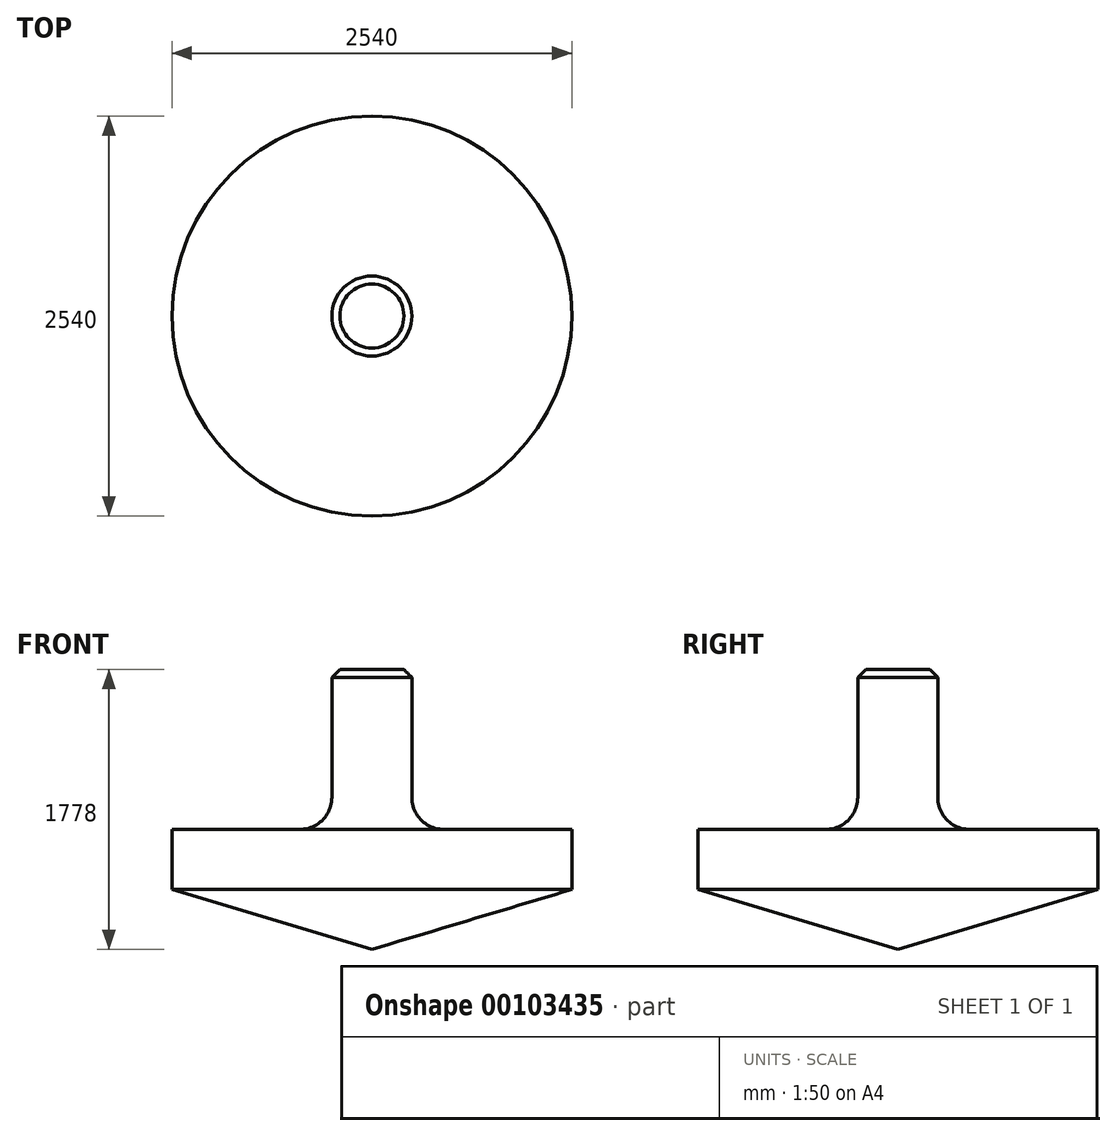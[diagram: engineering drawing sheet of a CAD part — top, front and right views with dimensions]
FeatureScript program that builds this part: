
annotation { "Feature Type Name" : "Feature", "Feature Type Description" : "" }
export const myFeature = defineFeature(function(context is Context, id is Id, definition is map)
    precondition{}
    {
        {
            var Q0;
            Q0=qCreatedBy(makeId("Front.planeOp"),FACE);
            var sketch = newSketch(context, id + "F0", { "sketchPlane" : qUnion([Q0])});
            skLineSegment(sketch, "E0", {"start": v(0, 1778) * mm, "end": v(0, -1437.3) * mm, "construction": true});
            skLineSegment(sketch, "E1", {"start": v(0, 1778) * mm, "end": v(254, 1778) * mm});
            skLineSegment(sketch, "E2", {"start": v(254, 1778) * mm, "end": v(254, 965.2) * mm});
            skLineSegment(sketch, "E3", {"start": v(457.2, 762) * mm, "end": v(1270, 762) * mm});
            skLineSegment(sketch, "E4", {"start": v(1270, 762) * mm, "end": v(1270, 381) * mm});
            skLineSegment(sketch, "E5", {"start": v(1270, 381) * mm, "end": v(0, 0) * mm});
            skLineSegment(sketch, "E6", {"start": v(0, 1778) * mm, "end": v(0, 0) * mm});
            skPoint(sketch, "E7.start.orphan", {"position": v(1270, 0) * mm});
            skPoint(sketch, "E8.visualSharp", {"position": v(254, 762) * mm});
            skArc(sketch, "E8.filletArc", {"start": v(254, 965.2) * mm, "mid": v(313.52, 821.52) * mm, "end": v(457.2, 762) * mm});
            skSolve(sketch);
        }
        {
            var Q0;
            Q0=makeQuery(id+"F0.imprint","IMPRINT",FACE,{"disambiguationData":[TD([[makeQuery(id+"F0.imprint","IMPRINT",EDGE,{"derivedFrom":sQuery(id+"F0.wireOp",EDGE,"E1")}),-1.0]])]});
            var Q1;
            Q1=sQuery(id+"F0.wireOp",EDGE,"E0");
            revolve(context, id + "F1", {"entities" : qUnion([Q0]), "axis" : qUnion([Q1]), "revolveType" : RevolveType.FULL});
        }
        {
            var Q0;
            Q0=makeQuery(id+"F1.opRevolve","SWEPT_EDGE",EDGE,{"disambiguationData":[OSD([sQuery(id+"F0.wireOp",EDGE,"E1"),sQuery(id+"F0.wireOp",EDGE,"E2")])]});
            chamfer(context, id + "F2", {"entities" : qUnion([Q0]), "width" : 50.8 * mm, "tangentPropagation" : true});
        }
    });
